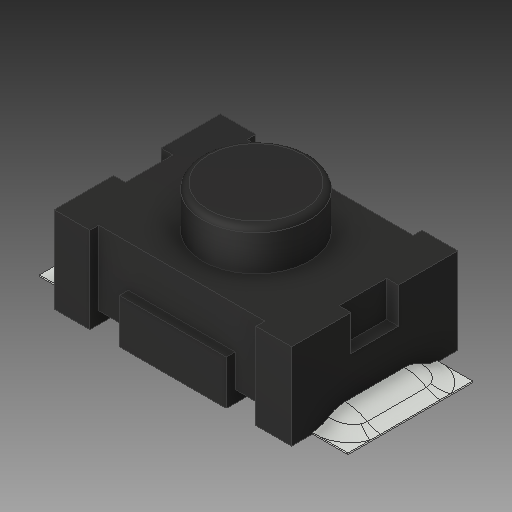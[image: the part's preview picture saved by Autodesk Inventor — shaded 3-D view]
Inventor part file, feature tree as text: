
AUTODESK INVENTOR PART (.ipt)
format: ipt  version: 2019.4 (Build 234330000, 330)  size: 211,968 bytes
history: native  units: mm
features: fillet x1
ambient origin geometry x8: Origin, YZ Plane, XZ Plane, XY Plane, X Axis, Y Axis, Z Axis, Center Point
bodies: Solid1 (feature_tree)
feature tree (1):
  fillet  "Fillet3"  [1 undecoded]
note: 1 required parameter value undecoded (feature->parameter linkage not recoverable at this tier; creation-order binding heuristic only, values carry confidence <= 0.55)
